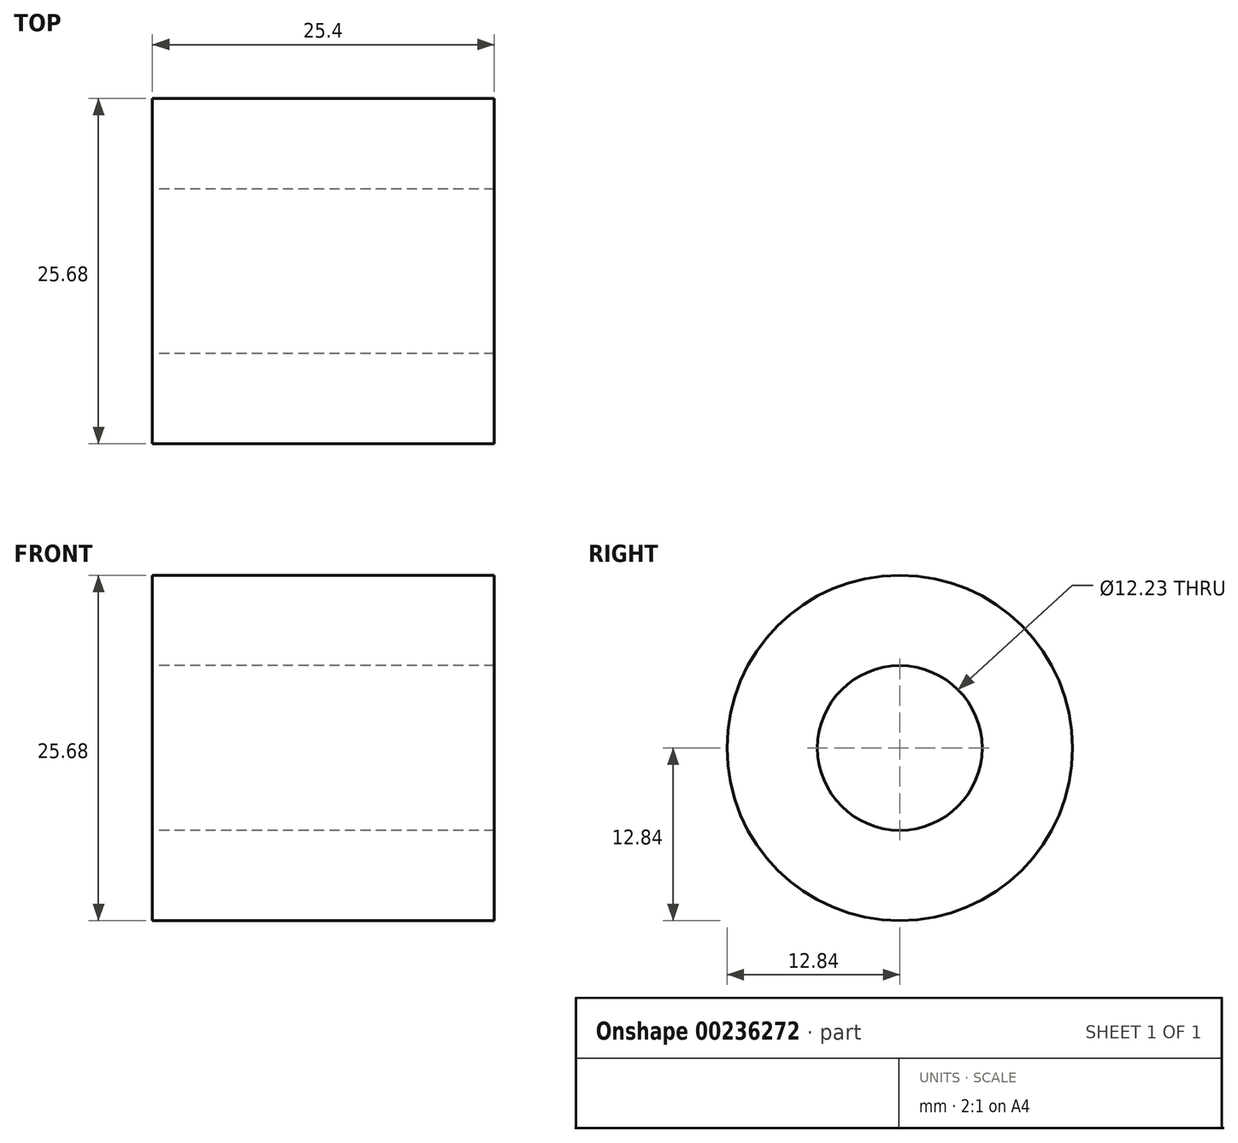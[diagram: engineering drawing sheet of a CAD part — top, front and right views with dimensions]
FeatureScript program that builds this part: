
annotation { "Feature Type Name" : "Feature", "Feature Type Description" : "" }
export const myFeature = defineFeature(function(context is Context, id is Id, definition is map)
    precondition{}
    {
        {
            var Q0;
            Q0=qCreatedBy(makeId("Right.planeOp"),FACE);
            var sketch = newSketch(context, id + "F0", { "sketchPlane" : qUnion([Q0])});
            skCircle(sketch, "E0", {"center": v(0, 0) * mm, "radius": 12.84 * mm});
            skCircle(sketch, "E1", {"center": v(0, 0) * mm, "radius": 6.11 * mm});
            skSolve(sketch);
        }
        {
            var Q0;
            Q0=makeQuery(id+"F0.imprint","IMPRINT",FACE,{"disambiguationData":[TD([[makeQuery(id+"F0.imprint","IMPRINT",EDGE,{"derivedFrom":sQuery(id+"F0.wireOp",EDGE,"E0")}),1.0]])]});
            extrude(context, id + "F1", {"entities" : qUnion([Q0]), "depth" : 25.4 * mm});
        }
    });
